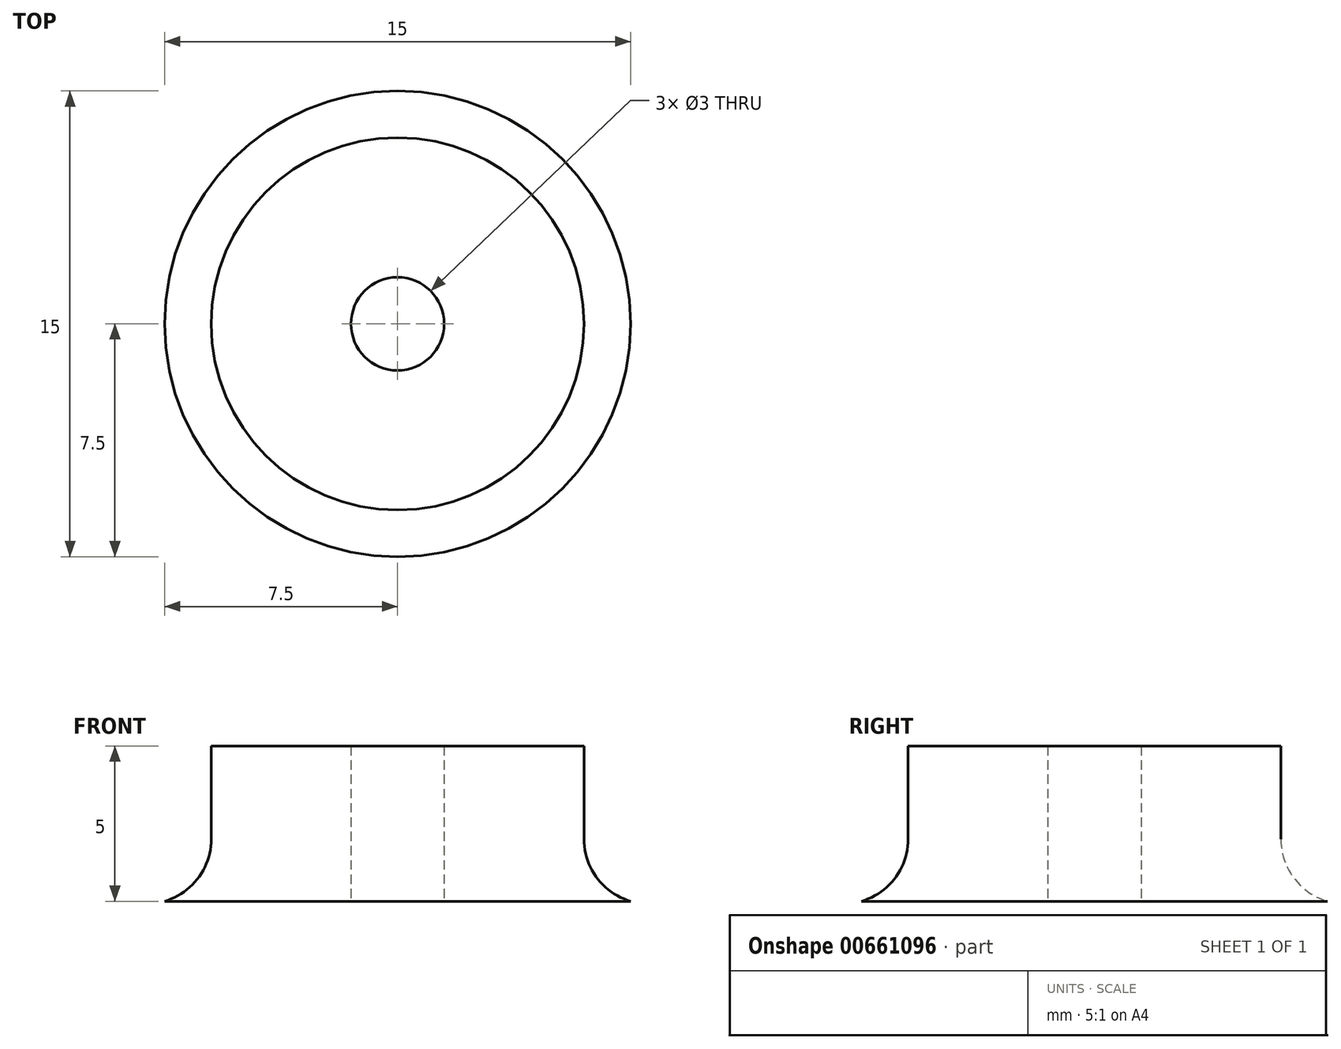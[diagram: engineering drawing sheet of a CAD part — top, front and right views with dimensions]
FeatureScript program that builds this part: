
annotation { "Feature Type Name" : "Feature", "Feature Type Description" : "" }
export const myFeature = defineFeature(function(context is Context, id is Id, definition is map)
    precondition{}
    {
        {
            var Q0;
            Q0=qCreatedBy(makeId("Front.planeOp"),FACE);
            var sketch = newSketch(context, id + "F0", { "sketchPlane" : qUnion([Q0])});
            skLineSegment(sketch, "E0", {"start": v(0, 0) * mm, "end": v(0, 5) * mm});
            skLineSegment(sketch, "E1", {"start": v(0, 0) * mm, "end": v(-7.5, 0) * mm});
            skLineSegment(sketch, "E2", {"start": v(0, 0) * mm, "end": v(-1.5, 0) * mm, "construction": true});
            skLineSegment(sketch, "E3", {"start": v(-1.5, 0) * mm, "end": v(-1.5, 5) * mm});
            skLineSegment(sketch, "E4", {"start": v(-1.5, 5) * mm, "end": v(-6, 5) * mm});
            skLineSegment(sketch, "E5", {"start": v(-7.5, 0) * mm, "end": v(-6, 0) * mm, "construction": true});
            skLineSegment(sketch, "E6", {"start": v(-6, 0) * mm, "end": v(-6, 2) * mm, "construction": true});
            skLineSegment(sketch, "E7", {"start": v(-6, 2) * mm, "end": v(-6, 5) * mm});
            skArc(sketch, "E8", {"start": v(-7.5, 0) * mm, "mid": v(-6.42, 0.75) * mm, "end": v(-6, 2) * mm});
            skSolve(sketch);
        }
        {
            var Q0;
            Q0 = qSketchRegion(id + "F0", true);
            var Q1;
            Q1=sQuery(id+"F0.wireOp",EDGE,"E0");
            revolve(context, id + "F1", {"entities" : qUnion([Q0]), "axis" : qUnion([Q1]), "revolveType" : RevolveType.FULL});
        }
    });
